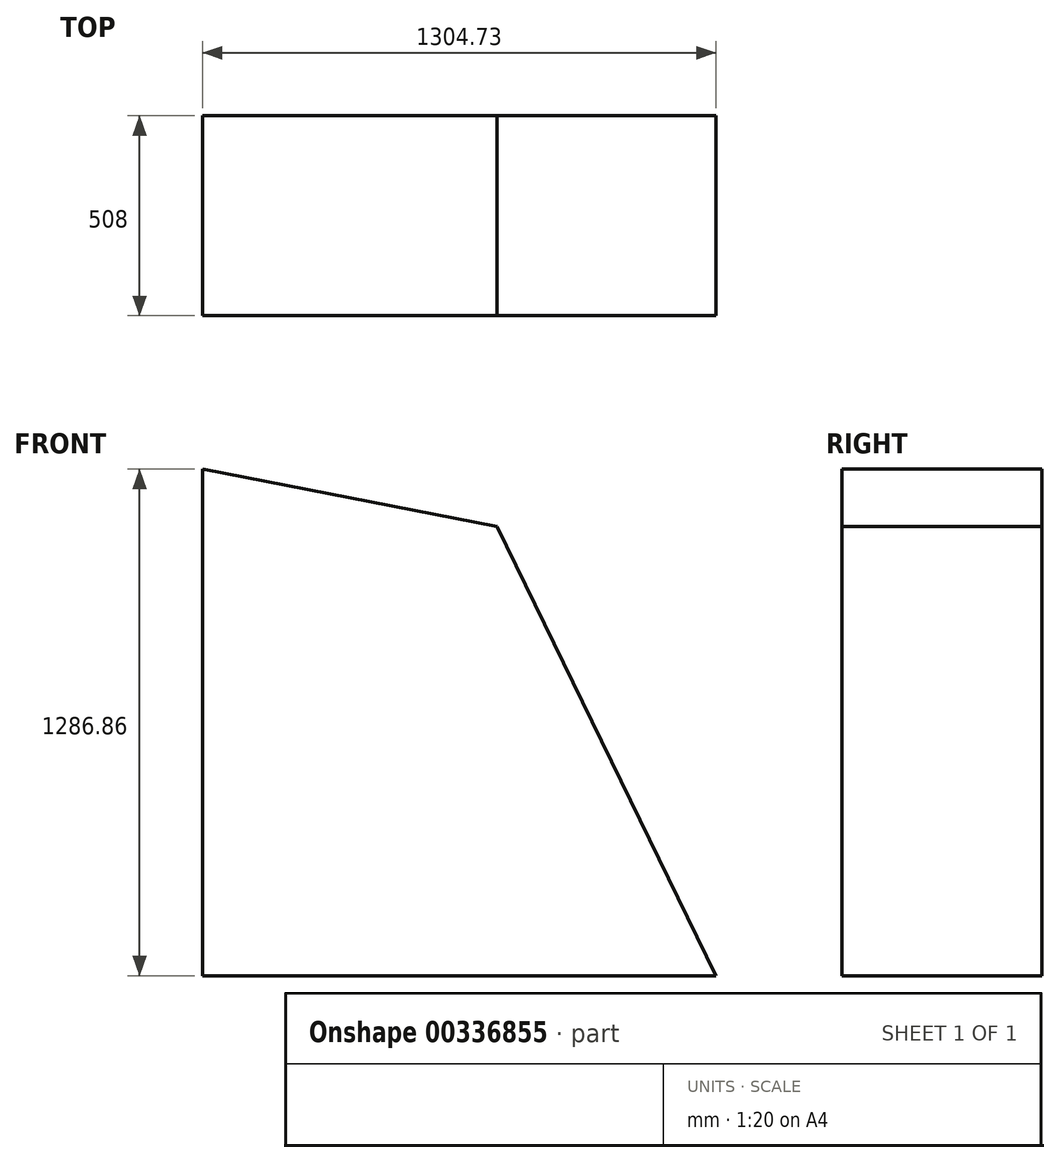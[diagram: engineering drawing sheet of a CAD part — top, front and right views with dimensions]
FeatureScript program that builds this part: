
annotation { "Feature Type Name" : "Feature", "Feature Type Description" : "" }
export const myFeature = defineFeature(function(context is Context, id is Id, definition is map)
    precondition{}
    {
        {
            var Q0;
            Q0=qCreatedBy(makeId("Front.planeOp"),FACE);
            var sketch = newSketch(context, id + "F0", { "sketchPlane" : qUnion([Q0])});
            skLineSegment(sketch, "E0", {"start": v(0, 0) * mm, "end": v(0, 1286.86) * mm});
            skLineSegment(sketch, "E1", {"start": v(0, 1286.86) * mm, "end": v(748, 1141.47) * mm});
            skLineSegment(sketch, "E2", {"start": v(748, 1141.47) * mm, "end": v(1304.73, 0) * mm});
            skLineSegment(sketch, "E3", {"start": v(1304.73, 0) * mm, "end": v(0, 0) * mm});
            skSolve(sketch);
        }
        {
            var Q0;
            Q0 = qSketchRegion(id + "F0", true);
            extrude(context, id + "F1", {"entities" : qUnion([Q0]), "depth" : 508 * mm});
        }
    });
